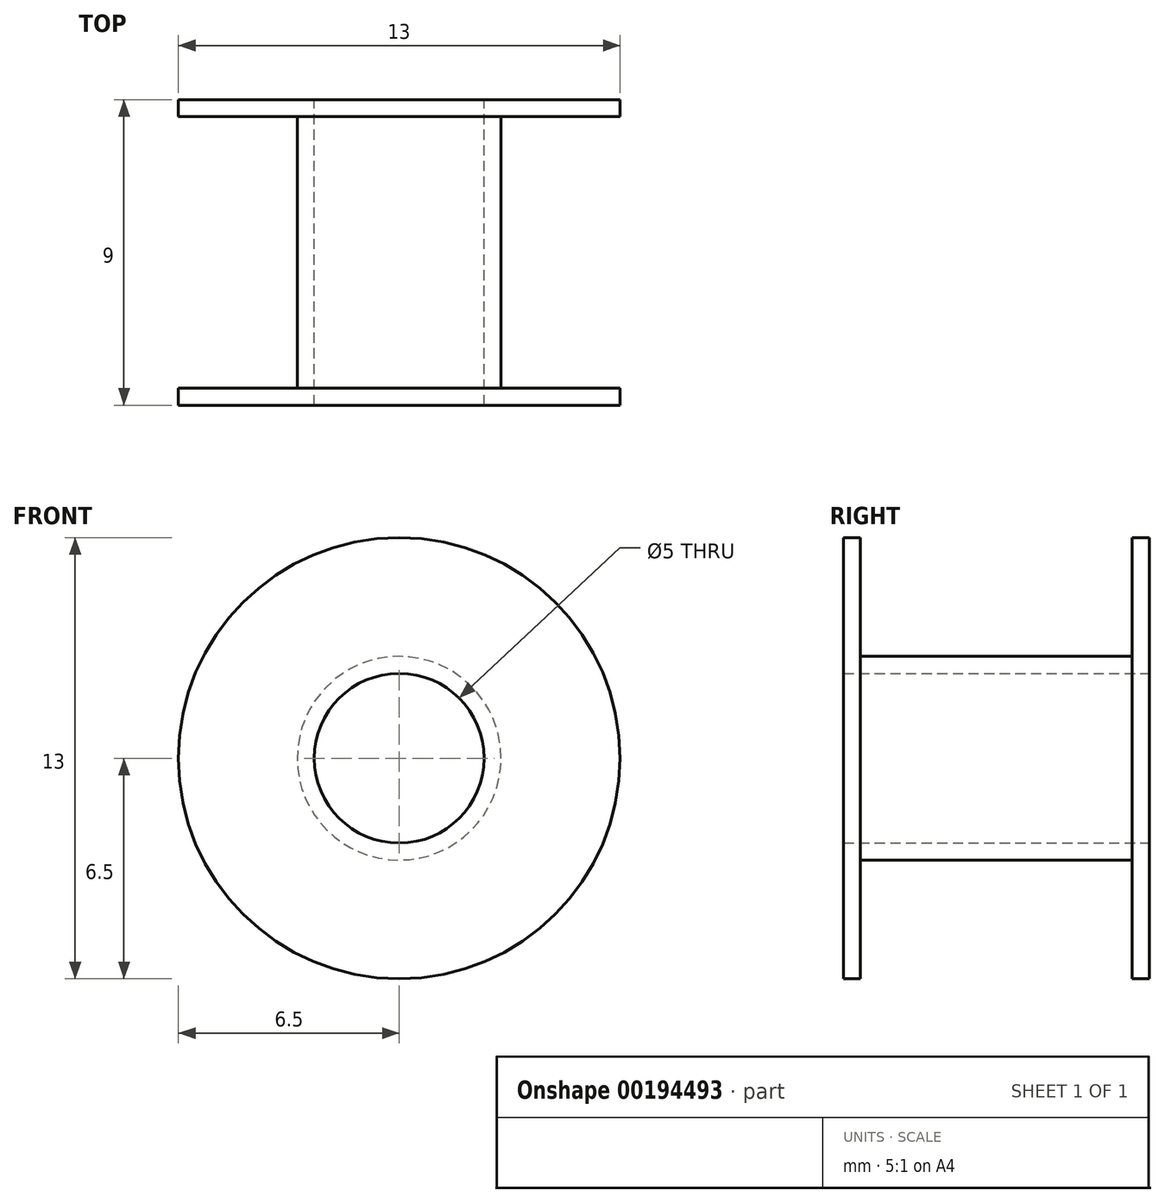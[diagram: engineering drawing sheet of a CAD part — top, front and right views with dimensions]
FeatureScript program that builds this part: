
annotation { "Feature Type Name" : "Feature", "Feature Type Description" : "" }
export const myFeature = defineFeature(function(context is Context, id is Id, definition is map)
    precondition{}
    {
        {
            var Q0;
            Q0=qCreatedBy(makeId("Front.planeOp"),FACE);
            var sketch = newSketch(context, id + "F0", { "sketchPlane" : qUnion([Q0])});
            skCircle(sketch, "E0", {"center": v(0, 0) * mm, "radius": 6.5 * mm});
            skCircle(sketch, "E1", {"center": v(0, 0) * mm, "radius": 2.5 * mm});
            skSolve(sketch);
        }
        {
            var Q0;
            Q0 = qSketchRegion(id + "F0", true);
            extrude(context, id + "F1", {"entities" : qUnion([Q0]), "depth" : .5 * mm, "offsetDistance" : 25.4 * mm});
        }
        {
            var Q0;
            Q0=makeQuery(id+"F1.opExtrude","CAP_FACE",FACE,{"disambiguationData":[OSD([sQuery(id+"F0.wireOp",EDGE,"E0"),sQuery(id+"F0.wireOp",EDGE,"E1")])],"isStart":false});
            var sketch = newSketch(context, id + "F2", { "sketchPlane" : qUnion([Q0])});
            skCircle(sketch, "E2", {"center": v(0, 0) * mm, "radius": 3 * mm});
            skSolve(sketch);
        }
        {
            var Q0;
            Q0=makeQuery(id+"F2.imprint","IMPRINT",FACE,{"disambiguationData":[TD([[makeQuery(id+"F2.imprint","IMPRINT",EDGE,{"derivedFrom":sQuery(id+"F2.wireOp",EDGE,"E2")}),1.0]])]});
            extrude(context, id + "F3", {"entities" : qUnion([Q0]), "operationType" : NewBodyOperationType.ADD, "depth" : 8 * mm, "offsetDistance" : 25.4 * mm});
        }
        {
            var Q0;
            Q0=makeQuery(id+"F3.opExtrude","CAP_FACE",FACE,{"disambiguationData":[OSD([sQuery(id+"F0.wireOp",EDGE,"E1"),sQuery(id+"F2.wireOp",EDGE,"E2")])],"isStart":false});
            var sketch = newSketch(context, id + "F4", { "sketchPlane" : qUnion([Q0])});
            skCircle(sketch, "E3", {"center": v(0, 0) * mm, "radius": 6.5 * mm});
            skCircle(sketch, "E4", {"center": v(0, 0) * mm, "radius": 2.5 * mm});
            skSolve(sketch);
        }
        {
            var Q0;
            Q0=makeQuery(id+"F4.imprint","IMPRINT",FACE,{"disambiguationData":[TD([[makeQuery(id+"F4.imprint","IMPRINT",EDGE,{"derivedFrom":sQuery(id+"F4.wireOp",EDGE,"E3")}),1.0]])]});
            var Q1;
            Q1=makeQuery(id+"F4.imprint","IMPRINT",FACE,{"disambiguationData":[TD([[makeQuery(id+"F4.imprint","IMPRINT",EDGE,{"derivedFrom":sQuery(id+"F4.wireOp",EDGE,"E4")}),-1.0]])]});
            extrude(context, id + "F5", {"entities" : qUnion([Q0, Q1]), "depth" : .5 * mm, "offsetDistance" : 25.4 * mm});
        }
        {
            var Q0;
            Q0=makeQuery(id+"F5.opExtrude","SWEPT_BODY",BODY,{"disambiguationData":[OSD([sQuery(id+"F4.wireOp",EDGE,"E3"),sQuery(id+"F4.wireOp",EDGE,"E4")])]});
            deleteBodies(context, id + "F6", {"entities" : qUnion([Q0])});
        }
        {
            var Q0;
            Q0=makeQuery(id+"F3.opExtrude","CAP_FACE",FACE,{"disambiguationData":[OSD([sQuery(id+"F0.wireOp",EDGE,"E1"),sQuery(id+"F2.wireOp",EDGE,"E2")])],"isStart":false});
            var sketch = newSketch(context, id + "F7", { "sketchPlane" : qUnion([Q0])});
            skCircle(sketch, "E5", {"center": v(0, 0) * mm, "radius": 2.5 * mm});
            skCircle(sketch, "E6", {"center": v(0, 0) * mm, "radius": 6.5 * mm});
            skSolve(sketch);
        }
        {
            var Q0;
            Q0 = qSketchRegion(id + "F7", true);
            extrude(context, id + "F8", {"entities" : qUnion([Q0]), "operationType" : NewBodyOperationType.ADD, "depth" : .5 * mm, "offsetDistance" : 25.4 * mm});
        }
    });
